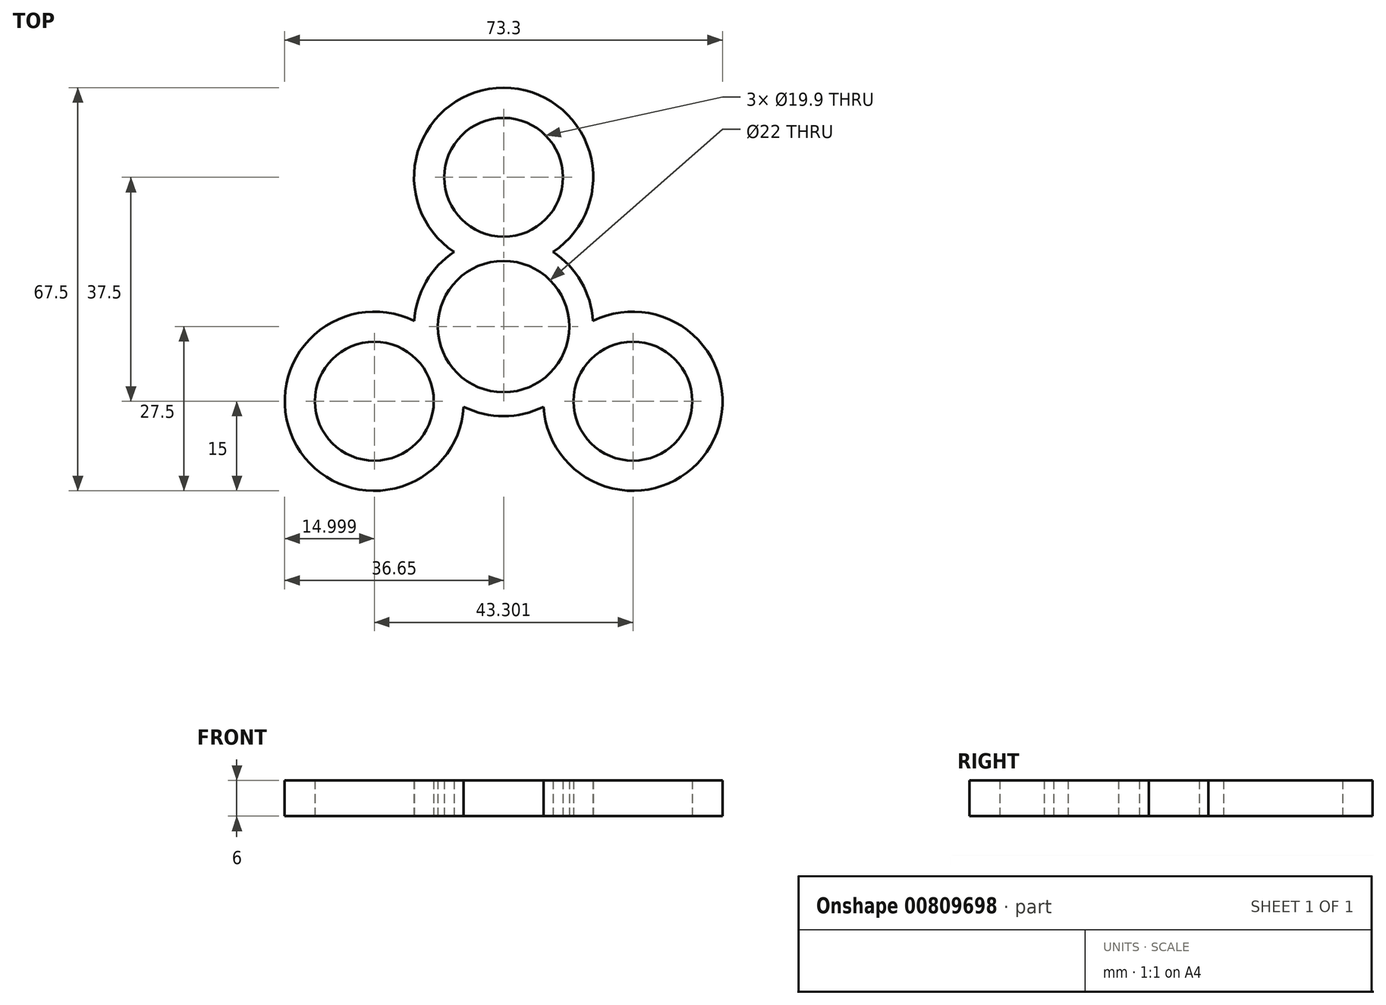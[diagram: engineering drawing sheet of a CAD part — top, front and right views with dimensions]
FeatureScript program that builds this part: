
annotation { "Feature Type Name" : "Feature", "Feature Type Description" : "" }
export const myFeature = defineFeature(function(context is Context, id is Id, definition is map)
    precondition{}
    {
        {
            var Q0;
            Q0=qCreatedBy(makeId("Top.planeOp"),FACE);
            var sketch = newSketch(context, id + "F0", { "sketchPlane" : qUnion([Q0])});
            skArc(sketch, "E0", {"start": v(9.53, 5.5) * mm, "mid": v(0, 11) * mm, "end": v(-9.53, 5.5) * mm});
            skCircle(sketch, "E1", {"center": v(0, 25) * mm, "radius": 9.95 * mm});
            skArc(sketch, "E2", {"start": v(-8.3, 12.5) * mm, "mid": v(-10.93, 10.27) * mm, "end": v(-13, 7.5) * mm});
            skArc(sketch, "E3", {"start": v(8.3, 12.5) * mm, "mid": v(0, 40) * mm, "end": v(-8.3, 12.5) * mm});
            skArc(sketch, "E4.trimOffspring", {"start": v(13, 7.5) * mm, "mid": v(10.93, 10.27) * mm, "end": v(8.3, 12.5) * mm});
            skArc(sketch, "E5.1.0", {"start": v(-14.97, 0.93) * mm, "mid": v(-34.64, -20) * mm, "end": v(-6.68, -13.43) * mm});
            skCircle(sketch, "E5.1.1", {"center": v(-21.65, -12.5) * mm, "radius": 9.95 * mm});
            skArc(sketch, "E5.1.2", {"start": v(-9.53, 5.5) * mm, "mid": v(-9.53, -5.5) * mm, "end": v(0, -11) * mm});
            skArc(sketch, "E5.1.3", {"start": v(-13, 7.5) * mm, "mid": v(-14.36, 4.33) * mm, "end": v(-14.97, 0.93) * mm});
            skArc(sketch, "E5.1.4", {"start": v(-6.68, -13.43) * mm, "mid": v(-3.43, -14.6) * mm, "end": v(0, -15) * mm});
            skArc(sketch, "E5.2.0", {"start": v(6.68, -13.43) * mm, "mid": v(34.64, -20) * mm, "end": v(14.97, 0.93) * mm});
            skCircle(sketch, "E5.2.1", {"center": v(21.65, -12.5) * mm, "radius": 9.95 * mm});
            skArc(sketch, "E5.2.2", {"start": v(0, -11) * mm, "mid": v(9.53, -5.5) * mm, "end": v(9.53, 5.5) * mm});
            skArc(sketch, "E5.2.3", {"start": v(0, -15) * mm, "mid": v(3.43, -14.6) * mm, "end": v(6.68, -13.43) * mm});
            skArc(sketch, "E5.2.4", {"start": v(14.97, 0.93) * mm, "mid": v(14.36, 4.33) * mm, "end": v(13, 7.5) * mm});
            skSolve(sketch);
        }
        {
            var Q0;
            Q0 = qSketchRegion(id + "F0", true);
            extrude(context, id + "F1", {"entities" : qUnion([Q0]), "depth" : 6 * mm, "offsetDistance" : 25 * mm});
        }
    });
